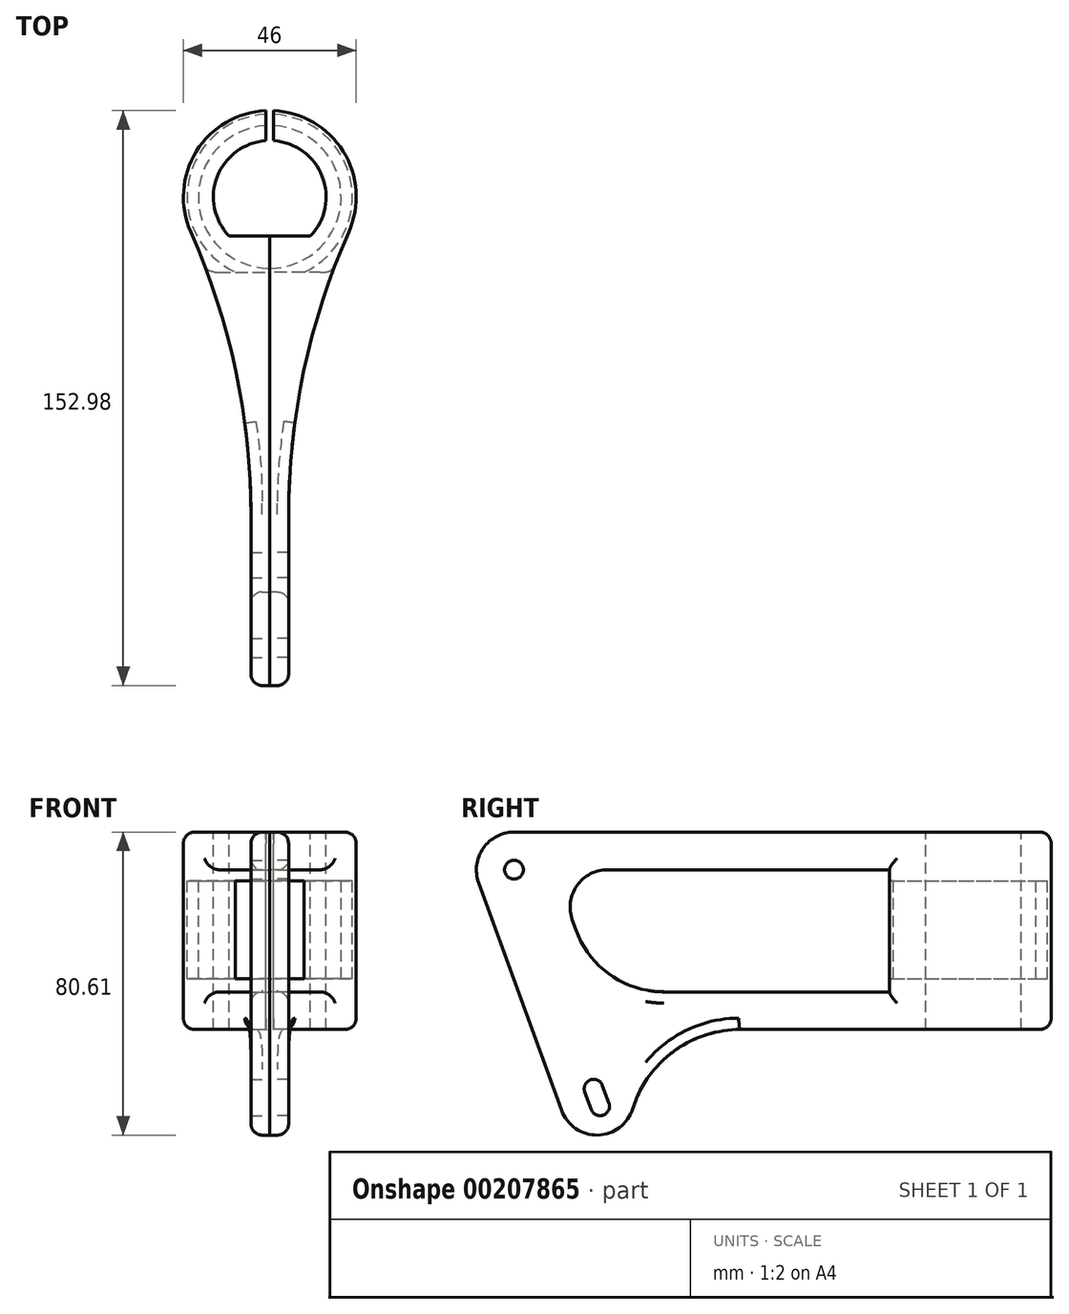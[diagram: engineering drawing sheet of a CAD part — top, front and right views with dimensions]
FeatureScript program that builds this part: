
annotation { "Feature Type Name" : "Feature", "Feature Type Description" : "" }
export const myFeature = defineFeature(function(context is Context, id is Id, definition is map)
    precondition{}
    {
        {
            var Q0;
            Q0=qCreatedBy(makeId("Top.planeOp"),FACE);
            var sketch = newSketch(context, id + "F0", { "sketchPlane" : qUnion([Q0])});
            skArc(sketch, "E0", {"start": v(10.8, -10.4) * mm, "mid": v(14, 5.41) * mm, "end": v(1, 14.97) * mm});
            skArc(sketch, "E1", {"start": v(21.03, -9.32) * mm, "mid": v(19.55, 12.12) * mm, "end": v(1, 22.98) * mm});
            skLineSegment(sketch, "E2", {"start": v(1, 14.97) * mm, "end": v(1, 22.98) * mm});
            skLineSegment(sketch, "E3", {"start": v(0, -10.4) * mm, "end": v(10.8, -10.4) * mm});
            skLineSegment(sketch, "E4", {"start": v(0, -10.4) * mm, "end": v(0, -170) * mm});
            skLineSegment(sketch, "E5", {"start": v(5, -170) * mm, "end": v(5, -85) * mm});
            skLineSegment(sketch, "E6", {"start": v(0, -170) * mm, "end": v(5, -170) * mm});
            skCircle(sketch, "E7", {"center": v(0, 0) * mm, "radius": 15 * mm, "construction": true});
            skArc(sketch, "E8", {"start": v(21.03, -9.32) * mm, "mid": v(9.05, -46.32) * mm, "end": v(5, -85) * mm});
            skSolve(sketch);
        }
        {
            var Q0;
            Q0 = qSketchRegion(id + "F0", true);
            extrude(context, id + "F1", {"entities" : qUnion([Q0]), "oppositeDirection" : true, "depth" : 100 * mm});
        }
        {
            var Q0;
            Q0=qCreatedBy(makeId("Right.planeOp"),FACE);
            var sketch = newSketch(context, id + "F2", { "sketchPlane" : qUnion([Q0])});
            skCircle(sketch, "E9", {"center": v(-120, -10) * mm, "radius": 2.5 * mm});
            skLineSegment(sketch, "E10", {"start": v(-120, -10) * mm, "end": v(-97.08, -72.96) * mm});
            skArc(sketch, "E11", {"start": v(-99.43, -73.81) * mm, "mid": v(-96.23, -75.3) * mm, "end": v(-94.74, -72.1) * mm});
            skLineSegment(sketch, "E12", {"start": v(-103.52, -26.05) * mm, "end": v(-104.47, -23.42) * mm});
            skLineSegment(sketch, "E13", {"start": v(-99.43, -73.81) * mm, "end": v(-101.14, -69.12) * mm});
            skLineSegment(sketch, "E14", {"start": v(-94.74, -72.1) * mm, "end": v(-96.45, -67.4) * mm});
            skLineSegment(sketch, "E15", {"start": v(-101.14, -69.12) * mm, "end": v(-96.45, -67.4) * mm, "construction": true});
            skArc(sketch, "E16", {"start": v(-96.45, -67.4) * mm, "mid": v(-99.65, -65.91) * mm, "end": v(-101.14, -69.12) * mm});
            skCircle(sketch, "E17", {"center": v(-97.94, -70.61) * mm, "radius": 9.64 * mm, "construction": true});
            skLineSegment(sketch, "E18", {"start": v(-20, -10) * mm, "end": v(-20, -42.5) * mm});
            skLineSegment(sketch, "E19", {"start": v(-20, -10) * mm, "end": v(-95.08, -10) * mm});
            skLineSegment(sketch, "E20", {"start": v(-170, -100) * mm, "end": v(-170, 0) * mm});
            skLineSegment(sketch, "E21", {"start": v(-80.02, -42.5) * mm, "end": v(-20, -42.5) * mm});
            skLineSegment(sketch, "E22", {"start": v(-104.47, -23.42) * mm, "end": v(-103.52, -26.05) * mm, "construction": true});
            skLineSegment(sketch, "E23", {"start": v(22.98, -100) * mm, "end": v(-170, -100) * mm});
            skLineSegment(sketch, "E24", {"start": v(-120, 0) * mm, "end": v(-170, 0) * mm});
            skArc(sketch, "E25", {"start": v(-103.52, -26.05) * mm, "mid": v(-94.36, -37.98) * mm, "end": v(-80.02, -42.5) * mm});
            skArc(sketch, "E26", {"start": v(-95.08, -10) * mm, "mid": v(-103.27, -14.26) * mm, "end": v(-104.47, -23.42) * mm});
            skLineSegment(sketch, "E27.trimOffspring", {"start": v(-129.4, -13.42) * mm, "end": v(-107.34, -74.03) * mm});
            skLineSegment(sketch, "E28", {"start": v(-59.75, -52.5) * mm, "end": v(22.98, -52.5) * mm});
            skLineSegment(sketch, "E29", {"start": v(22.98, -52.5) * mm, "end": v(22.98, -100.1) * mm});
            skArc(sketch, "E30", {"start": v(-59.75, -52.5) * mm, "mid": v(-77.53, -58.34) * mm, "end": v(-88.4, -73.58) * mm});
            skArc(sketch, "E31.trimOffspring", {"start": v(-107.34, -74.03) * mm, "mid": v(-97.7, -80.6) * mm, "end": v(-88.4, -73.58) * mm});
            skArc(sketch, "E32", {"start": v(-120, 0) * mm, "mid": v(-128.2, -4.26) * mm, "end": v(-129.4, -13.42) * mm});
            skSolve(sketch);
        }
        {
            var Q0;
            Q0 = qSketchRegion(id + "F2", true);
            extrude(context, id + "F3", {"entities" : qUnion([Q0]), "operationType" : NewBodyOperationType.REMOVE, "endBound" : BoundingType.THROUGH_ALL, "depth" : 25 * mm});
        }
        {
            var Q0;
            Q0=qCreatedBy(makeId("Right.planeOp"),FACE);
            var sketch = newSketch(context, id + "F4", { "sketchPlane" : qUnion([Q0])});
            skLineSegment(sketch, "E33.bottom", {"start": v(-22, -13) * mm, "end": v(-19, -13) * mm});
            skLineSegment(sketch, "E33.top", {"start": v(-22, -39) * mm, "end": v(-19, -39) * mm});
            skLineSegment(sketch, "E33.left", {"start": v(-22, -13) * mm, "end": v(-22, -39) * mm});
            skLineSegment(sketch, "E33.right", {"start": v(-19, -13) * mm, "end": v(-19, -39) * mm});
            skLineSegment(sketch, "E34", {"start": v(0, -3.56) * mm, "end": v(0, -220.77) * mm, "construction": true});
            skLineSegment(sketch, "E35", {"start": v(-19, -13) * mm, "end": v(-19, -209.57) * mm, "construction": true});
            skSolve(sketch);
        }
        {
            var Q0;
            Q0 = qSketchRegion(id + "F4", true);
            var Q1;
            Q1=sQuery(id+"F4.wireOp",EDGE,"E34");
            var Q2;
            Q2=sQuery(id+"F4.wireOp",EDGE,"E34");
            revolve(context, id + "F5", {"operationType" : NewBodyOperationType.REMOVE, "entities" : qUnion([Q0]), "surfaceEntities" : qUnion([Q1]), "axis" : qUnion([Q2]), "revolveType" : RevolveType.FULL});
        }
        {
            var Q0;
            Q0=makeQuery(id+"F3.boolean.opBoolean","INTERSECT",EDGE,{"derivedFrom":[makeQuery(id+"F1.opExtrude","SWEPT_FACE",FACE,{"disambiguationData":[OSD([sQuery(id+"F0.wireOp",EDGE,"E5")])]}),makeQuery(id+"F3.opExtrude","SWEPT_FACE",FACE,{"disambiguationData":[OSD([sQuery(id+"F2.wireOp",EDGE,"E27.trimOffspring")])]})]});
            var Q1;
            Q1=makeQuery(id+"F3.boolean.opBoolean","INTERSECT",EDGE,{"derivedFrom":[makeQuery(id+"F1.opExtrude","SWEPT_FACE",FACE,{"disambiguationData":[OSD([sQuery(id+"F0.wireOp",EDGE,"E8")])]}),makeQuery(id+"F3.opExtrude","SWEPT_FACE",FACE,{"disambiguationData":[OSD([sQuery(id+"F2.wireOp",EDGE,"E21")])]})]});
            var Q2;
            Q2=makeQuery(id+"F3.boolean.opBoolean","INTERSECT",EDGE,{"derivedFrom":[makeQuery(id+"F1.opExtrude","SWEPT_FACE",FACE,{"disambiguationData":[OSD([sQuery(id+"F0.wireOp",EDGE,"E8")])]}),makeQuery(id+"F3.opExtrude","SWEPT_FACE",FACE,{"disambiguationData":[OSD([sQuery(id+"F2.wireOp",EDGE,"E18")])]})]});
            fillet(context, id + "F6", {"entities" : qUnion([Q0, Q1, Q2]), "radius" : 3 * mm, "tangentPropagation" : true, "allowEdgeOverflow" : false});
        }
        {
            var Q0;
            Q0=makeQuery(id+"F1.opExtrude","SWEPT_BODY",BODY,{"disambiguationData":[OSD([sQuery(id+"F0.wireOp",EDGE,"E0"),sQuery(id+"F0.wireOp",EDGE,"E1"),sQuery(id+"F0.wireOp",EDGE,"E2"),sQuery(id+"F0.wireOp",EDGE,"E3"),sQuery(id+"F0.wireOp",EDGE,"E4"),sQuery(id+"F0.wireOp",EDGE,"E5"),sQuery(id+"F0.wireOp",EDGE,"E6")])]});
            var Q1;
            Q1=qCreatedBy(makeId("Right.planeOp"),FACE);
            mirror(context, id + "F7", {"entities" : qUnion([Q0]), "mirrorPlane" : qUnion([Q1])});
        }
    });
